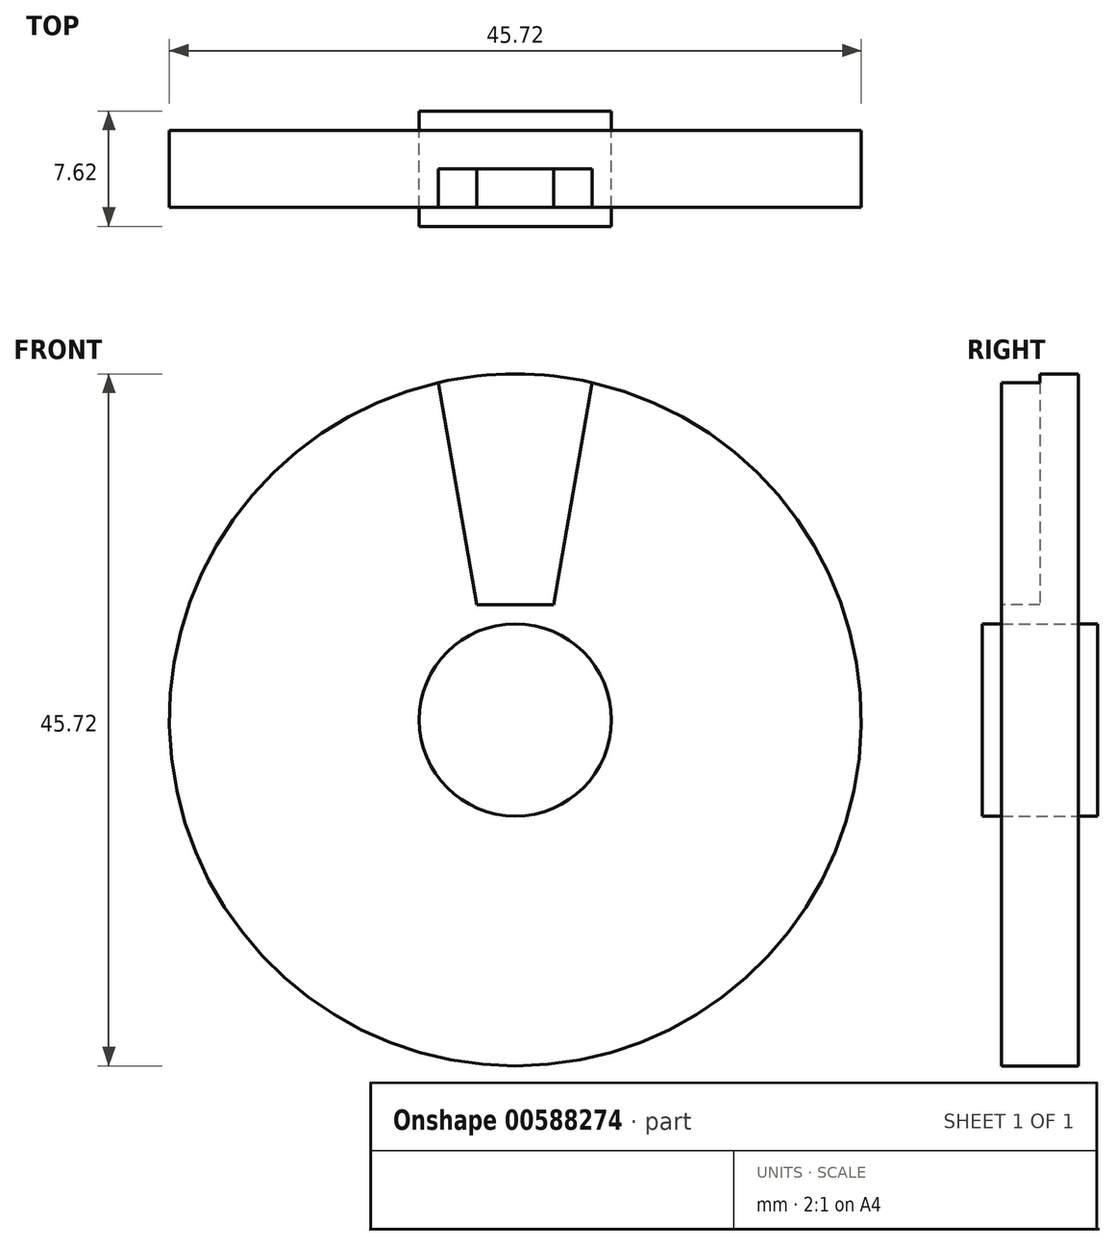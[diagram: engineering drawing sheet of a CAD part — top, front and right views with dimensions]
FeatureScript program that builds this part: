
annotation { "Feature Type Name" : "Feature", "Feature Type Description" : "" }
export const myFeature = defineFeature(function(context is Context, id is Id, definition is map)
    precondition{}
    {
        {
            var Q0;
            Q0=qCreatedBy(makeId("Front.planeOp"),FACE);
            var sketch = newSketch(context, id + "F0", { "sketchPlane" : qUnion([Q0])});
            skCircle(sketch, "E0", {"center": v(0, 0) * mm, "radius": 6.35 * mm});
            skSolve(sketch);
        }
        {
            var Q0;
            Q0=qCreatedBy(makeId("Front.planeOp"),FACE);
            var sketch = newSketch(context, id + "F1", { "sketchPlane" : qUnion([Q0])});
            skCircle(sketch, "E1", {"center": v(0, 0) * mm, "radius": 22.86 * mm});
            skSolve(sketch);
        }
        {
            var Q0;
            Q0=qSketchRegion(id+"F0",true);
            extrude(context, id + "F2", {"entities" : qUnion([Q0]), "endBound" : BoundingType.SYMMETRIC, "depth" : 7.62 * mm});
        }
        {
            var Q0;
            Q0=makeQuery(id+"F1.imprint","IMPRINT",FACE,{"disambiguationData":[TD([[makeQuery(id+"F1.imprint","IMPRINT",EDGE,{"derivedFrom":sQuery(id+"F1.wireOp",EDGE,"E1")}),1.0]])]});
            extrude(context, id + "F3", {"entities" : qUnion([Q0]), "endBound" : BoundingType.SYMMETRIC, "depth" : 5.08 * mm});
        }
        {
            var Q0;
            Q0=makeQuery(id+"F3.opExtrude","CAP_FACE",FACE,{"disambiguationData":[OSD([sQuery(id+"F1.wireOp",EDGE,"E1")])],"isStart":false});
            var sketch = newSketch(context, id + "F4", { "sketchPlane" : qUnion([Q0])});
            skLineSegment(sketch, "E2", {"start": v(-2.54, 7.62) * mm, "end": v(2.54, 7.62) * mm});
            skLineSegment(sketch, "E3", {"start": v(-5.08, 22.29) * mm, "end": v(-2.54, 7.62) * mm});
            skLineSegment(sketch, "E4", {"start": v(5.08, 22.29) * mm, "end": v(2.54, 7.62) * mm});
            skSolve(sketch);
        }
        {
            var Q0;
            Q0=makeQuery(id+"F4.imprint","IMPRINT",FACE,{"disambiguationData":[TD([[makeQuery(id+"F4.imprint","IMPRINT",EDGE,{"derivedFrom":sQuery(id+"F4.wireOp",EDGE,"E2")}),1.0]])]});
            extrude(context, id + "F5", {"entities" : qUnion([Q0]), "operationType" : NewBodyOperationType.REMOVE, "oppositeDirection" : true, "depth" : 2.54 * mm});
        }
    });
